# Revit family: HWO230_Revit
name_source: partatom
category: Specialty Equipment
revit_build: Autodesk Revit MEP 2014 (Build: 20130308_1515(x64)
units: mm (PartAtom-declared; Revit-internal decimal feet)

## types (1)
- HWO230
    10-KEY PAD = YES
    AUTOMATIC HOLD = YES
    BAKE ELEMENT = 3,000W - 8 PASS
    BROIL ELEMENT = 3,500W - 8 PASS
    BROIL-ROASTING PAN SET = AORPVR
    CHILD LOCK = YES
    CIRCUIT BREAKER (A) = 50
    CLEANING TYPE = SELF CLEAN & GREENCLEAN™
    CLOCK = YES
    CONVECTION ELEMENT = 2,200W
    CONVECTION TYPE = PURE CONVECTION™
    COOKIE SHEETS (SET OF 3) = ACSRO303
    COOKING MODES BOTH CAVITIES = PURE CONVECTION™ CONVECTION BAKE CONVECTION BROIL CONVECTION ROAST BAKE BROIL
    DEHYDRATE = YES
    DELAY TIME COOKING = YES
    Depth = 23 5/8"
    Description = 30-INCH DOUBLE WALL OVEN HERITAGE COLLECTION
    Door = Stainless Steel
    Door Glass = Glass
    ENERGY SOURCE = ELECTRIC
    FREQUENCY (HZ) = 60
    GLIDERACK™ = 2 (UPPER) / 2 (LOWER)
    Handle = Stainless Steel
    Height = 50 1/8"
    KEEP WARM = YES
    LIGHTING = HALOGEN
    LIMITED, PARTS AND LABOR = 1 YEAR
    Manufacturer = Dacor
    Model = HWO230
    PIZZA STONE = ABS16
    PROOF = YES
    RACK POSITIONS = 7
    SABBATH MODE = YES
    STANDARD RACK = 1 (UPPER) / 1 (LOWER)
    Support = Plastic-Black
    TEMPERATURE PROBE = 1
    TIMED COOKING = YES
    TWO TIMERS = YES
    Unit = Stainless Steel
    VOLTS (V) = 240
    Width = 29 7/8"

## geometry (parser evidence)
native form markers: Sweep x1
no freeform markers — native parametric forms only
